# Revit family: Plum Fix_Basin_Argent_Mode 550 SemiRecessed
name_source: partatom
category: Plumbing Fixtures
revit_build: Autodesk Revit 2016 (Build: 20190508_0715(x64)
units: mm (PartAtom-declared; Revit-internal decimal feet)

## family parameters
Always vertical = Yes
Cut with Voids When Loaded = Yes
OmniClass Number = 23.45.05.14.14
OmniClass Title = Sinks/Lavatories
Part Type = Normal
Room Calculation Point = No
Round Connector Dimension = Use Diameter
Shared = No
Work Plane-Based = No

## types (4) — shared parameters
Body Material = z_Argent_Ceramic White
CW Connection = No
Description = Mode 550 Semi Recessed Basin
HW Connection = No
IfcExportAs = IfcSanitaryTerminal
IfcExportType = WASHHANDBASIN
Manufacturer = Argent
Manufacturer_Overall Depth = 425 mm
Manufacturer_Overall Height = 130 mm
Manufacturer_Overall Width = 550 mm
Manufacturer_URL__Product Specific = https://www.argentaust.com.au
ModifiedIssue_ANZRS = 20200422 $
URL = https://www.argentaust.com.au
Uniclass2015Code = Pr_40_20_96_70
Uniclass2015Title = Recessed washbasins
Uniclass2015Version = Products v1.17
Vent Connection = No
Waste Connection = Yes
zero-valued in all types: Cost

## per-type parameters (varying)
| type | LeftSoapDispenser | LeftTapHole | LeftTapHoleHeight | Manufacturer_Spec Code | Model | RightSoapDispenser | RightTapHole | RightTapHoleHeight | Type Comments |
| 1 Tap Hole (FC14TUL01) | No | No | 15 mm | FC14TUL01 | FC14TUL01 | No | No | 15 mm | 1 Tap Hole |
| 1 Tap Hole w. Soap LHS (FC14TUL01SDL) | Yes | Yes | 130 mm | FC14TUL01SDL | FC14TUL01SDL | No | No | 15 mm | 1 Tap Hole w. Soap Dispenser LHS |
| 1 Tap Hole w. Soap RHS (FC14TUL01SDR) | No | No | 15 mm | FC14TUL01SDR | FC14TUL01SDR | Yes | Yes | 130 mm | 1 Tap Hole w. Soap Dispenser RHS |
| 3 Tap Hole (FC14TUL07) | No | Yes | 130 mm | FC14TUL07 | FC14TUL07 | No | Yes | 130 mm | 3 Tap Hole |

## geometry (parser evidence)
native form markers: Sweep x7
no freeform markers — native parametric forms only
